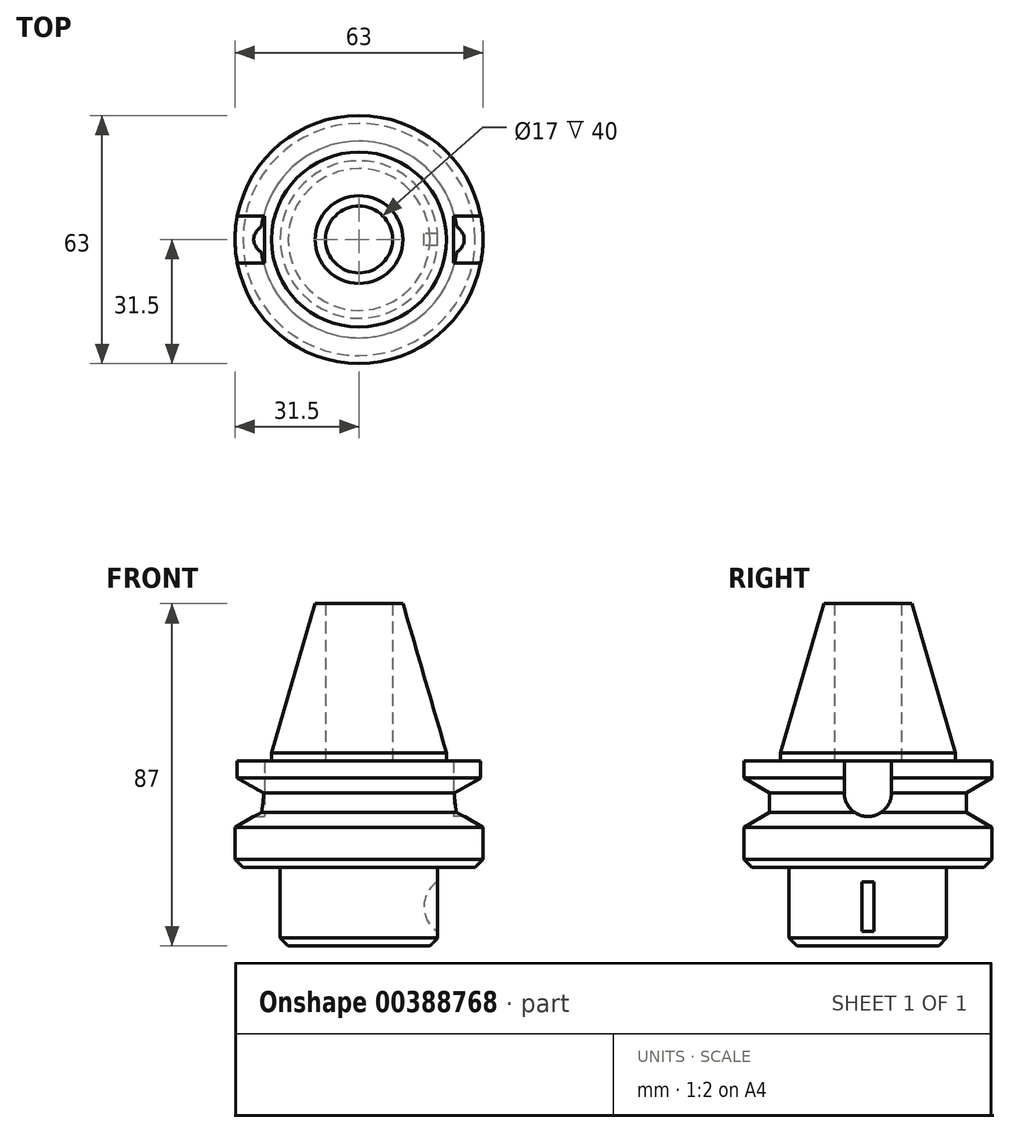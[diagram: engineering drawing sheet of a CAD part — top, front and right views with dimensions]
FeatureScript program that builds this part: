
annotation { "Feature Type Name" : "Feature", "Feature Type Description" : "" }
export const myFeature = defineFeature(function(context is Context, id is Id, definition is map)
    precondition{}
    {
        {
            var Q0;
            Q0=qCreatedBy(makeId("Front.planeOp"),FACE);
            var sketch = newSketch(context, id + "F0", { "sketchPlane" : qUnion([Q0])});
            skLineSegment(sketch, "E0.bottom", {"start": v(0, 0) * mm, "end": v(22.23, 0) * mm});
            skLineSegment(sketch, "E0.top", {"start": v(0, 40) * mm, "end": v(22.22, 40) * mm, "construction": true});
            skLineSegment(sketch, "E0.left", {"start": v(0, 0) * mm, "end": v(0, 40) * mm});
            skLineSegment(sketch, "E0.right", {"start": v(22.23, 0) * mm, "end": v(22.22, 40) * mm, "construction": true});
            skLineSegment(sketch, "E1", {"start": v(0, 50.27) * mm, "end": v(0, -51.48) * mm, "construction": true});
            skLineSegment(sketch, "E2", {"start": v(22.23, 0) * mm, "end": v(22.23, 2) * mm});
            skLineSegment(sketch, "E3", {"start": v(22.23, 2) * mm, "end": v(11.15, 40) * mm});
            skLineSegment(sketch, "E4", {"start": v(11.15, 40) * mm, "end": v(0, 40) * mm});
            skLineSegment(sketch, "E5.bottom", {"start": v(0, 0) * mm, "end": v(31.5, 0) * mm});
            skLineSegment(sketch, "E5.top", {"start": v(0, -4.35) * mm, "end": v(31.5, -4.35) * mm});
            skLineSegment(sketch, "E5.left", {"start": v(0, 0) * mm, "end": v(0, -4.35) * mm});
            skLineSegment(sketch, "E5.right", {"start": v(31.5, 0) * mm, "end": v(31.5, -4.35) * mm});
            skLineSegment(sketch, "E6.bottom", {"start": v(0, -8.1) * mm, "end": v(25, -8.1) * mm});
            skLineSegment(sketch, "E6.top", {"start": v(0, -13.1) * mm, "end": v(25, -13.1) * mm});
            skLineSegment(sketch, "E6.left", {"start": v(0, -8.1) * mm, "end": v(0, -13.1) * mm});
            skLineSegment(sketch, "E6.right", {"start": v(25, -8.1) * mm, "end": v(25, -13.1) * mm});
            skLineSegment(sketch, "E7.bottom", {"start": v(0, -16.85) * mm, "end": v(31.5, -16.85) * mm});
            skLineSegment(sketch, "E7.top", {"start": v(0, -27) * mm, "end": v(31.5, -27) * mm});
            skLineSegment(sketch, "E7.left", {"start": v(0, -16.85) * mm, "end": v(0, -27) * mm});
            skLineSegment(sketch, "E7.right", {"start": v(31.5, -16.85) * mm, "end": v(31.5, -27) * mm});
            skLineSegment(sketch, "E8", {"start": v(31.5, -4.35) * mm, "end": v(25, -8.1) * mm});
            skLineSegment(sketch, "E9", {"start": v(25, -13.1) * mm, "end": v(31.5, -16.85) * mm});
            skLineSegment(sketch, "E10", {"start": v(0, -4.35) * mm, "end": v(0, -27) * mm});
            skLineSegment(sketch, "E11.bottom", {"start": v(0, -27) * mm, "end": v(20, -27) * mm});
            skLineSegment(sketch, "E11.top", {"start": v(0, -47) * mm, "end": v(20, -47) * mm});
            skLineSegment(sketch, "E11.left", {"start": v(0, -27) * mm, "end": v(0, -47) * mm});
            skLineSegment(sketch, "E11.right", {"start": v(20, -27) * mm, "end": v(20, -47) * mm});
            skSolve(sketch);
        }
        {
            var Q0;
            Q0 = qSketchRegion(id + "F0", true);
            var Q1;
            Q1=sQuery(id+"F0.wireOp",EDGE,"E1");
            revolve(context, id + "F1", {"entities" : qUnion([Q0]), "axis" : qUnion([Q1]), "revolveType" : RevolveType.FULL});
        }
        {
            var Q0;
            Q0=makeQuery(id+"F1.opRevolve","SWEPT_EDGE",EDGE,{"disambiguationData":[OSD([sQuery(id+"F0.wireOp",EDGE,"E7.top"),sQuery(id+"F0.wireOp",EDGE,"E7.right")])]});
            var Q1;
            Q1=makeQuery(id+"F1.opRevolve","SWEPT_EDGE",EDGE,{"disambiguationData":[OSD([sQuery(id+"F0.wireOp",EDGE,"E11.top"),sQuery(id+"F0.wireOp",EDGE,"E11.right")])]});
            chamfer(context, id + "F2", {"entities" : qUnion([Q0, Q1]), "width" : 2 * mm, "tangentPropagation" : true});
        }
        {
            var Q0;
            Q0=qCreatedBy(makeId("Right.planeOp"),FACE);
            cPlane(context, id + "F3", {"entities" : qUnion([Q0]), "cplaneType" : CPlaneType.OFFSET, "offset" : 24 * mm, "width" : 150 * mm, "height" : 150 * mm});
        }
        {
            var Q0;
            Q0=qCreatedBy(id+"F3.planeOp",FACE);
            var sketch = newSketch(context, id + "F4", { "sketchPlane" : qUnion([Q0])});
            skLineSegment(sketch, "E12", {"start": v(0, 0) * mm, "end": v(0, -55.72) * mm, "construction": true});
            skCircle(sketch, "E13", {"center": v(0, -8.1) * mm, "radius": 6 * mm});
            skLineSegment(sketch, "E14.bottom", {"start": v(0, 0) * mm, "end": v(31.5, 0) * mm, "construction": true});
            skLineSegment(sketch, "E14.top", {"start": v(0, -4.35) * mm, "end": v(31.5, -4.35) * mm, "construction": true});
            skLineSegment(sketch, "E14.left", {"start": v(0, 0) * mm, "end": v(0, -4.35) * mm, "construction": true});
            skLineSegment(sketch, "E14.right", {"start": v(31.5, 0) * mm, "end": v(31.5, -4.35) * mm, "construction": true});
            skLineSegment(sketch, "E15", {"start": v(31.5, -4.35) * mm, "end": v(25, -8.1) * mm, "construction": true});
            skLineSegment(sketch, "E16", {"start": v(25, -8.1) * mm, "end": v(25, -13.1) * mm, "construction": true});
            skLineSegment(sketch, "E17", {"start": v(25, -13.1) * mm, "end": v(31.5, -16.85) * mm, "construction": true});
            skLineSegment(sketch, "E18", {"start": v(31.5, -16.85) * mm, "end": v(0, -16.85) * mm, "construction": true});
            skLineSegment(sketch, "E19", {"start": v(25, -10.6) * mm, "end": v(0, -10.6) * mm, "construction": true});
            skLineSegment(sketch, "E20", {"start": v(25, -8.1) * mm, "end": v(0, -8.1) * mm, "construction": true});
            skLineSegment(sketch, "E21", {"start": v(6, -8.1) * mm, "end": v(-6, -8.1) * mm, "construction": true});
            skLineSegment(sketch, "E22", {"start": v(-6, -8.1) * mm, "end": v(-6, 0) * mm});
            skLineSegment(sketch, "E23", {"start": v(-6, 0) * mm, "end": v(6, 0) * mm});
            skLineSegment(sketch, "E24", {"start": v(6, 0) * mm, "end": v(6, -8.1) * mm});
            skSolve(sketch);
        }
        {
            var Q0;
            Q0 = qSketchRegion(id + "F4", true);
            extrude(context, id + "F5", {"entities" : qUnion([Q0]), "operationType" : NewBodyOperationType.REMOVE, "depth" : 63.53 * mm});
        }
        {
            var Q0;
            Q0=makeQuery(id+"F1.opRevolve","SWEPT_BODY",BODY,{"disambiguationData":[OSD([sQuery(id+"F0.wireOp",EDGE,"E0.left"),sQuery(id+"F0.wireOp",EDGE,"E2"),sQuery(id+"F0.wireOp",EDGE,"E3"),sQuery(id+"F0.wireOp",EDGE,"E4"),sQuery(id+"F0.wireOp",EDGE,"E5.bottom"),sQuery(id+"F0.wireOp",EDGE,"E5.left"),sQuery(id+"F0.wireOp",EDGE,"E5.right"),sQuery(id+"F0.wireOp",EDGE,"E6.right"),sQuery(id+"F0.wireOp",EDGE,"E7.top"),sQuery(id+"F0.wireOp",EDGE,"E7.right"),sQuery(id+"F0.wireOp",EDGE,"E8"),sQuery(id+"F0.wireOp",EDGE,"E9"),sQuery(id+"F0.wireOp",EDGE,"E10"),sQuery(id+"F0.wireOp",EDGE,"E11.top"),sQuery(id+"F0.wireOp",EDGE,"E11.left"),sQuery(id+"F0.wireOp",EDGE,"E11.right")])]});
            var Q1;
            Q1=qCreatedBy(makeId("Right.planeOp"),FACE);
            mirror(context, id + "F6", {"operationType" : NewBodyOperationType.INTERSECT, "entities" : qUnion([Q0]), "mirrorPlane" : qUnion([Q1])});
        }
        {
            var Q0;
            Q0=qCreatedBy(makeId("Front.planeOp"),FACE);
            var sketch = newSketch(context, id + "F7", { "sketchPlane" : qUnion([Q0])});
            skLineSegment(sketch, "E25", {"start": v(0, -61.47) * mm, "end": v(0, 0) * mm, "construction": true});
            skLineSegment(sketch, "E26", {"start": v(0, -27) * mm, "end": v(41.41, -27) * mm, "construction": true});
            skCircle(sketch, "E27", {"center": v(24, -37) * mm, "radius": 7.5 * mm});
            skSolve(sketch);
        }
        {
            var Q0;
            Q0 = qSketchRegion(id + "F7", true);
            extrude(context, id + "F8", {"entities" : qUnion([Q0]), "operationType" : NewBodyOperationType.REMOVE, "endBound" : BoundingType.SYMMETRIC, "depth" : 3 * mm});
        }
        {
            var Q0;
            Q0=qCreatedBy(makeId("Top.planeOp"),FACE);
            var sketch = newSketch(context, id + "F9", { "sketchPlane" : qUnion([Q0])});
            skCircle(sketch, "E28", {"center": v(0, 0) * mm, "radius": 8.5 * mm});
            skSolve(sketch);
        }
        {
            var Q0;
            Q0 = qSketchRegion(id + "F9", true);
            extrude(context, id + "F10", {"entities" : qUnion([Q0]), "operationType" : NewBodyOperationType.REMOVE, "depth" : 89.84 * mm});
        }
    });
